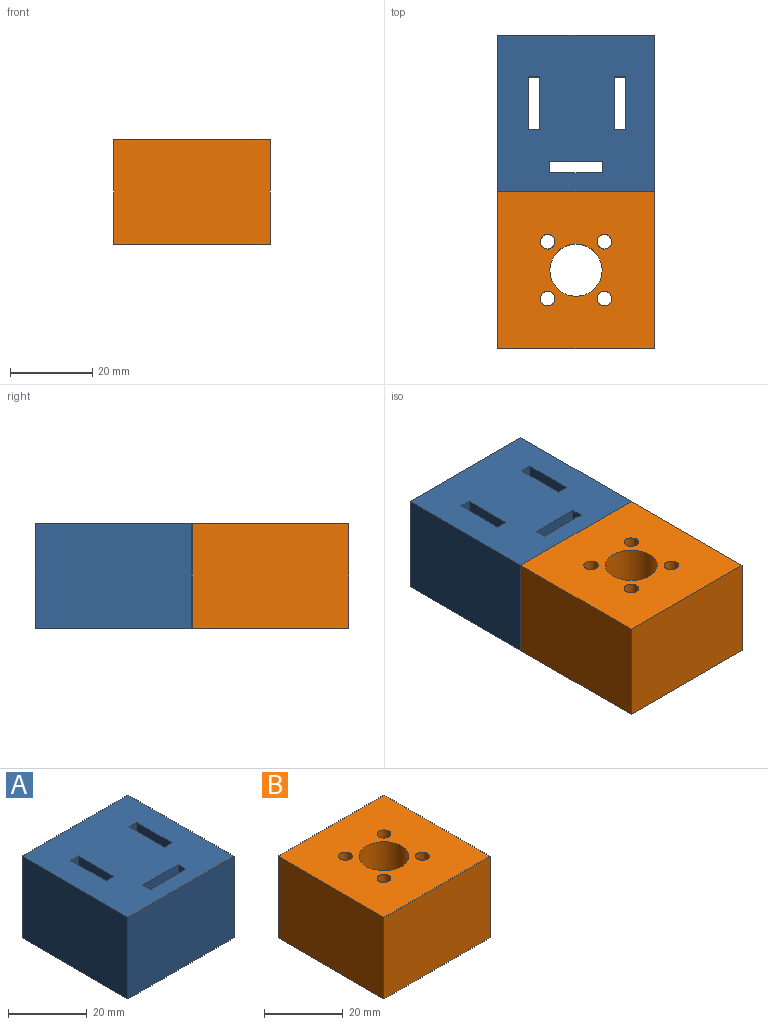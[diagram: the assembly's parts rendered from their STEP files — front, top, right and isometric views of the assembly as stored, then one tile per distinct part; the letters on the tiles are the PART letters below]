
ASSEMBLY  parts=2 mates=1
PART A: 18 faces, bbox 38.1x38.1x25.4 mm
  f0: plane 38.1x25.4mm, normal (-1,0,0), area 967.7mm2, adj f1,f15,f16,f17
  f1: plane 38.1x25.4mm, normal (0,-1,0), area 967.7mm2, adj f0,f2,f16,f17
  f2: plane 38.1x25.4mm, normal (1,0,0), area 967.7mm2, adj f1,f15,f16,f17
  f3: plane 25.4x12.7mm, normal (0,1,0), area 322.6mm2, adj f4,f12,f16,f17
  f4: plane 25.4x2.79mm, normal (1,0,0), area 71mm2, adj f3,f5,f16,f17
  f5: plane 25.4x12.7mm, normal (0,-1,0), area 322.6mm2, adj f4,f12,f16,f17
  f6: plane 25.4x2.79mm, normal (0,1,0), area 71mm2, adj f7,f13,f16,f17
  f7: plane 25.4x12.7mm, normal (1,0,0), area 322.6mm2, adj f6,f8,f16,f17
  f8: plane 25.4x2.79mm, normal (0,-1,0), area 71mm2, adj f7,f13,f16,f17
  f9: plane 25.4x2.79mm, normal (0,1,0), area 71mm2, adj f10,f14,f16,f17
  f10: plane 25.4x12.7mm, normal (1,0,0), area 322.6mm2, adj f9,f11,f16,f17
  f11: plane 25.4x2.79mm, normal (0,-1,0), area 71mm2, adj f10,f14,f16,f17
  f12: plane 25.4x2.79mm, normal (-1,0,0), area 71mm2, adj f3,f5,f16,f17
  f13: plane 25.4x12.7mm, normal (-1,0,0), area 322.6mm2, adj f6,f8,f16,f17
  f14: plane 25.4x12.7mm, normal (-1,0,0), area 322.6mm2, adj f9,f11,f16,f17
  f15: plane 38.1x25.4mm, normal (0,1,0), area 967.7mm2, adj f0,f2,f16,f17
  f16: plane 38.1x38.1mm, normal (0,0,1), area 1345.2mm2, adj f0,f1,f2,f3,f4,f5,f6,f7
  f17: plane 38.1x38.1mm, normal (0,0,-1), area 1345.2mm2, adj f0,f1,f2,f3,f4,f5,f6,f7
PART B: 11 faces, bbox 38.1x38.1x25.4 mm
  f0: plane 38.1x25.4mm, normal (-1,0,0), area 967.7mm2, adj f1,f8,f9,f10
  f1: plane 38.1x25.4mm, normal (0,-1,0), area 967.7mm2, adj f0,f2,f9,f10
  f2: plane 38.1x25.4mm, normal (1,0,0), area 967.7mm2, adj f1,f8,f9,f10
  f3: cylinder r=6.35mm len=25.4mm, axis (0,0,-1), area 1013.4mm2, adj f9,f10
  f4: cylinder r=1.78mm len=25.4mm, axis (0,0,-1), area 283.8mm2, adj f9,f10
  f5: cylinder r=1.78mm len=25.4mm, axis (0,0,-1), area 283.8mm2, adj f9,f10
  f6: cylinder r=1.78mm len=25.4mm, axis (0,0,-1), area 283.8mm2, adj f9,f10
  f7: cylinder r=1.78mm len=25.4mm, axis (0,0,-1), area 283.8mm2, adj f9,f10
  f8: plane 38.1x25.4mm, normal (0,1,0), area 967.7mm2, adj f0,f2,f9,f10
  f9: plane 38.1x38.1mm, normal (0,0,1), area 1285.2mm2, adj f0,f1,f2,f3,f4,f5,f6,f7
  f10: plane 38.1x38.1mm, normal (0,0,-1), area 1285.2mm2, adj f0,f1,f2,f3,f4,f5,f6,f7
PLACE A t=(-15.91,11.71,-0.13)mm
PLACE B rot(axis=(0,0,1),90deg) t=(-15.91,-26.39,-0.13)mm
MATE fastened B.f2 <-> A.f1  axis (0,1,0) through (-15.91,-7.34,12.57)mm
